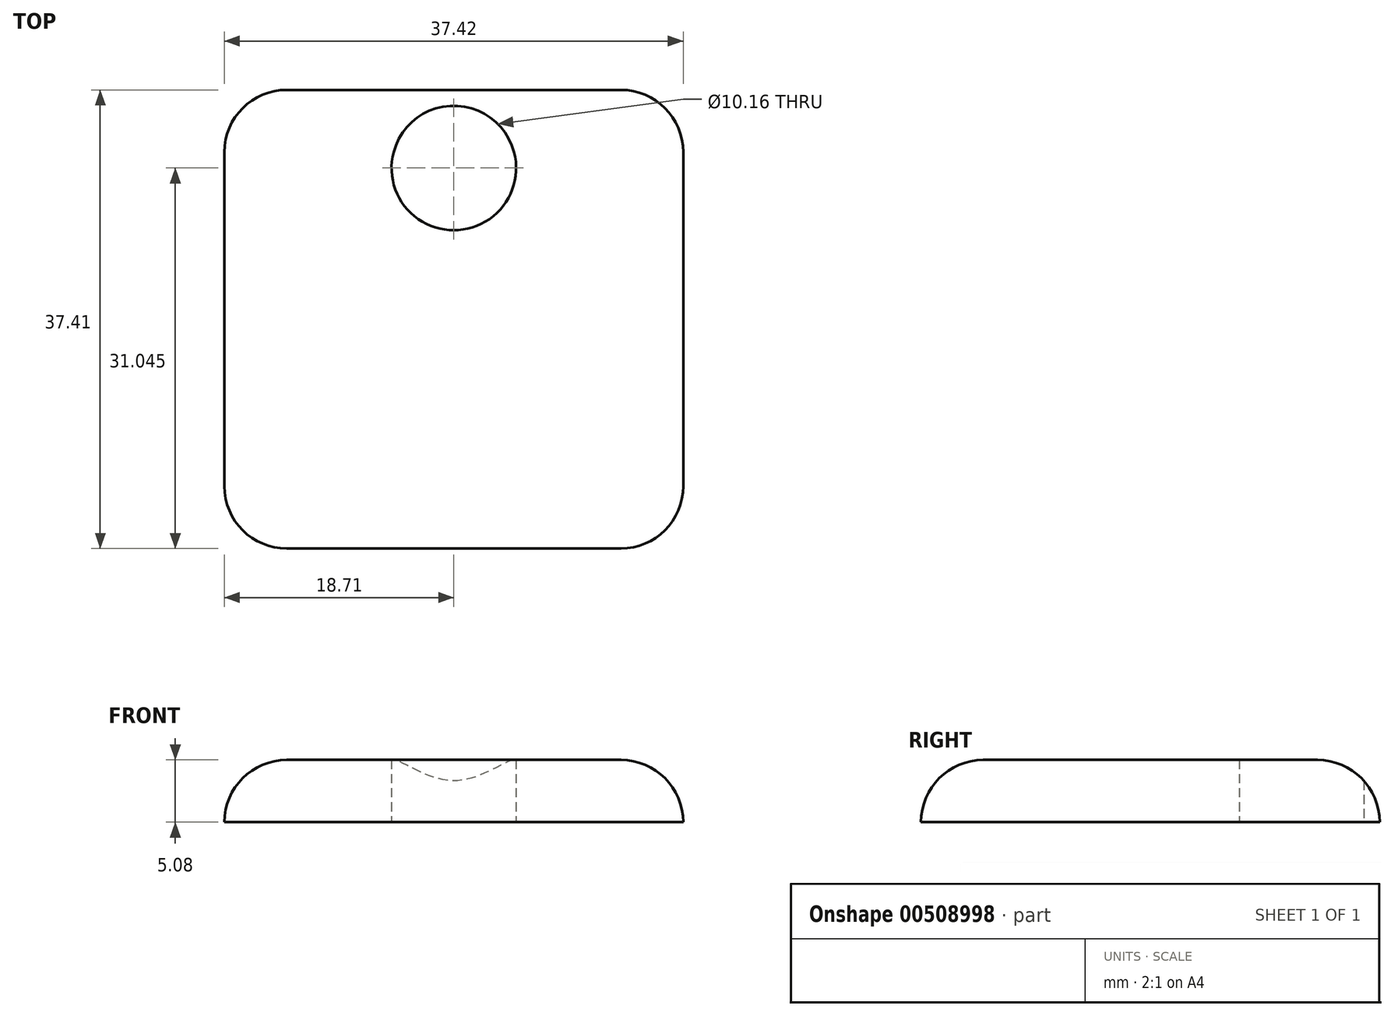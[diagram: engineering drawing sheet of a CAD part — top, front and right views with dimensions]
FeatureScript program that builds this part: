
annotation { "Feature Type Name" : "Feature", "Feature Type Description" : "" }
export const myFeature = defineFeature(function(context is Context, id is Id, definition is map)
    precondition{}
    {
        {
            var Q0;
            Q0=qCreatedBy(makeId("Top.planeOp"),FACE);
            var sketch = newSketch(context, id + "F0", { "sketchPlane" : qUnion([Q0])});
            skLineSegment(sketch, "E0.bottom", {"start": v(-44.7, 54.58) * mm, "end": v(-7.3, 54.58) * mm});
            skLineSegment(sketch, "E0.top", {"start": v(-44.7, 17.17) * mm, "end": v(-7.3, 17.17) * mm});
            skLineSegment(sketch, "E0.left", {"start": v(-44.7, 54.58) * mm, "end": v(-44.7, 17.17) * mm});
            skLineSegment(sketch, "E0.right", {"start": v(-7.3, 54.58) * mm, "end": v(-7.3, 17.17) * mm});
            skCircle(sketch, "E1", {"center": v(-26, 48.21) * mm, "radius": 5.08 * mm});
            skSolve(sketch);
        }
        {
            var Q0;
            Q0=makeQuery(id+"F0.imprint","IMPRINT",FACE,{"disambiguationData":[TD([[makeQuery(id+"F0.imprint","IMPRINT",EDGE,{"derivedFrom":sQuery(id+"F0.wireOp",EDGE,"E0.bottom")}),-1.0]])]});
            extrude(context, id + "F1", {"entities" : qUnion([Q0]), "depth" : 5.08 * mm});
        }
        {
            var Q0;
            Q0=makeQuery(id+"F1.opExtrude","CAP_EDGE",EDGE,{"disambiguationData":[OSD([sQuery(id+"F0.wireOp",EDGE,"E0.top")])],"isStart":false});
            fillet(context, id + "F2", {"entities" : qUnion([Q0]), "radius" : 5.08 * mm, "tangentPropagation" : true, "allowEdgeOverflow" : false});
        }
        {
            var Q0;
            Q0=makeQuery(id+"F1.opExtrude","CAP_EDGE",EDGE,{"disambiguationData":[OSD([sQuery(id+"F0.wireOp",EDGE,"E0.right")])],"isStart":false});
            fillet(context, id + "F3", {"entities" : qUnion([Q0]), "radius" : 5.08 * mm, "tangentPropagation" : true, "allowEdgeOverflow" : false});
        }
        {
            var Q0;
            Q0=makeQuery(id+"F1.opExtrude","CAP_EDGE",EDGE,{"disambiguationData":[OSD([sQuery(id+"F0.wireOp",EDGE,"E0.bottom")])],"isStart":false});
            fillet(context, id + "F4", {"entities" : qUnion([Q0]), "radius" : 5.08 * mm, "tangentPropagation" : true, "allowEdgeOverflow" : false});
        }
        {
            var Q0;
            Q0=makeQuery(id+"F1.opExtrude","CAP_EDGE",EDGE,{"disambiguationData":[OSD([sQuery(id+"F0.wireOp",EDGE,"E0.left")])],"isStart":false});
            fillet(context, id + "F5", {"entities" : qUnion([Q0]), "radius" : 5.08 * mm, "tangentPropagation" : true, "allowEdgeOverflow" : false});
        }
    });
